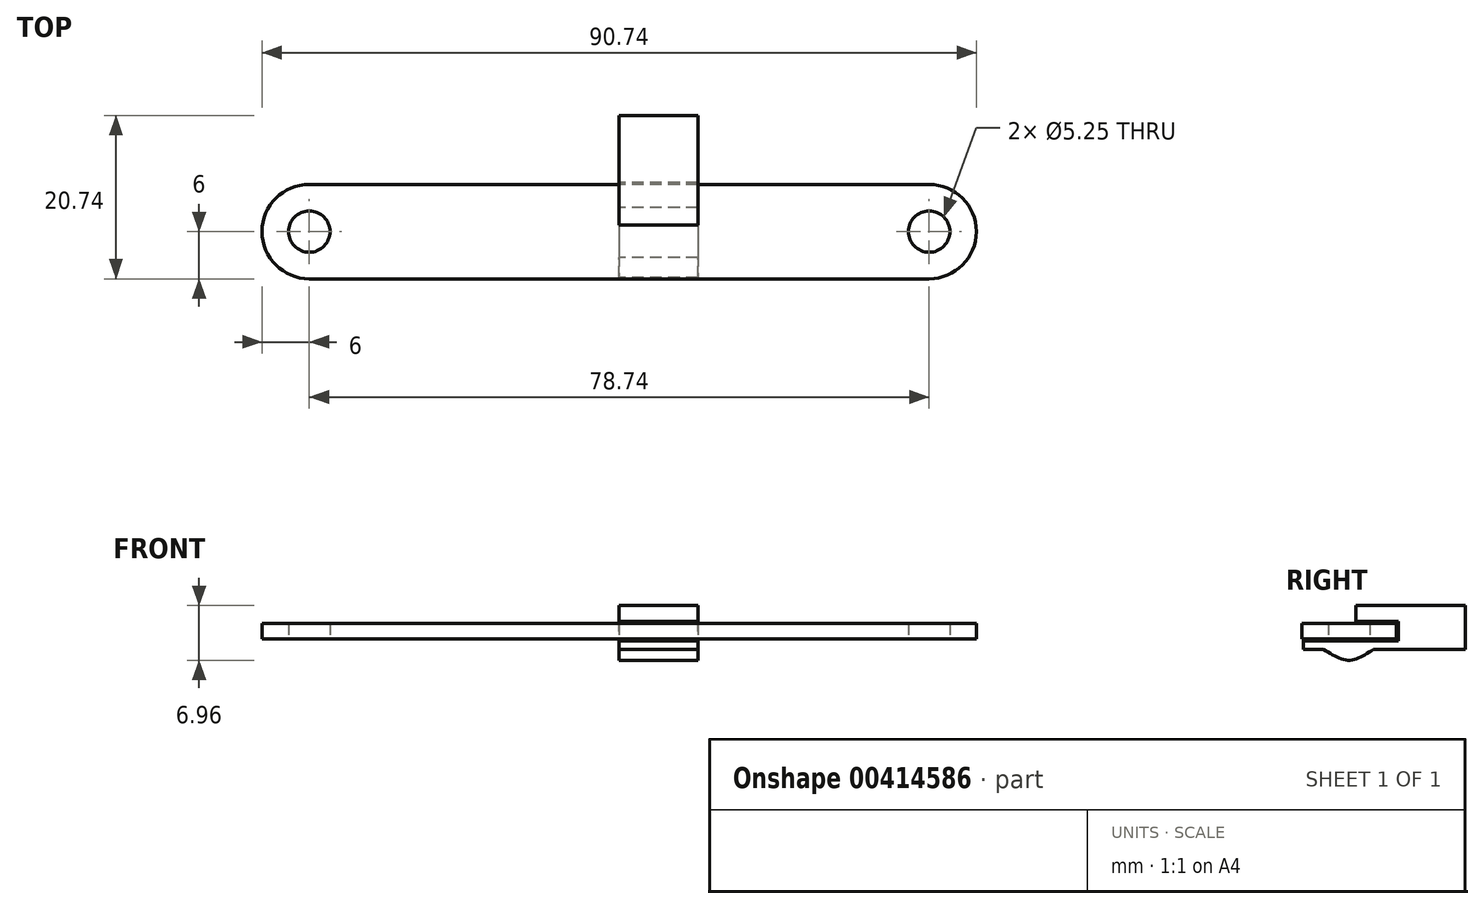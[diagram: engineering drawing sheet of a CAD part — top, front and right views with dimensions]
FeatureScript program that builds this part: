
annotation { "Feature Type Name" : "Feature", "Feature Type Description" : "" }
export const myFeature = defineFeature(function(context is Context, id is Id, definition is map)
    precondition{}
    {
        {
            var Q0;
            Q0=qCreatedBy(makeId("Top.planeOp"),FACE);
            var sketch = newSketch(context, id + "F0", { "sketchPlane" : qUnion([Q0])});
            skLineSegment(sketch, "E0.bottom", {"start": v(39.37, -6) * mm, "end": v(-39.37, -6) * mm});
            skLineSegment(sketch, "E0.top", {"start": v(39.37, 6) * mm, "end": v(-39.37, 6) * mm});
            skLineSegment(sketch, "E0.left", {"start": v(39.37, -6) * mm, "end": v(39.37, 6) * mm});
            skLineSegment(sketch, "E0.right", {"start": v(-39.37, -6) * mm, "end": v(-39.37, 6) * mm});
            skPoint(sketch, "E0.middle", {"position": v(0, 0) * mm});
            skCircle(sketch, "E1", {"center": v(-39.37, 0) * mm, "radius": 6 * mm});
            skCircle(sketch, "E2", {"center": v(39.37, 0) * mm, "radius": 6 * mm});
            skCircle(sketch, "E3", {"center": v(-39.37, 0) * mm, "radius": 2.62 * mm});
            skCircle(sketch, "E4", {"center": v(39.37, 0) * mm, "radius": 2.62 * mm});
            skSolve(sketch);
        }
        {
            var Q0;
            Q0 = qSketchRegion(id + "F0", true);
            extrude(context, id + "F1", {"entities" : qUnion([Q0]), "depth" : 2 * mm});
        }
        {
            var Q0;
            Q0=qCreatedBy(makeId("Right.planeOp"),FACE);
            var sketch = newSketch(context, id + "F2", { "sketchPlane" : qUnion([Q0])});
            skLineSegment(sketch, "E5", {"start": v(-5.85, -1.3) * mm, "end": v(14.74, -1.3) * mm});
            skLineSegment(sketch, "E6", {"start": v(14.74, -1.3) * mm, "end": v(14.74, 4.25) * mm});
            skLineSegment(sketch, "E7", {"start": v(14.74, 4.25) * mm, "end": v(0.86, 4.25) * mm});
            skLineSegment(sketch, "E8", {"start": v(0.86, 4.25) * mm, "end": v(0.86, 2.25) * mm});
            skLineSegment(sketch, "E9", {"start": v(0.86, 2.25) * mm, "end": v(6.25, 2.25) * mm});
            skLineSegment(sketch, "E10", {"start": v(6.25, 2.25) * mm, "end": v(6.25, -0.25) * mm});
            skLineSegment(sketch, "E11", {"start": v(6.25, -0.25) * mm, "end": v(-5.85, -0.25) * mm});
            skLineSegment(sketch, "E12", {"start": v(-5.85, -0.25) * mm, "end": v(-5.85, -1.3) * mm});
            skFitSpline(sketch, "E13", {"points": [v(3.08, -1.3) * mm, v(0, -2.7) * mm, v(-3.26, -1.3) * mm], "startDerivative": vector(-6.17, -4.22) * mm, "endDerivative": vector(-6.5, 4.18) * mm});
            skSolve(sketch);
        }
        {
            var Q0;
            Q0 = qSketchRegion(id + "F2", true);
            extrude(context, id + "F3", {"entities" : qUnion([Q0]), "depth" : 10 * mm});
        }
    });
